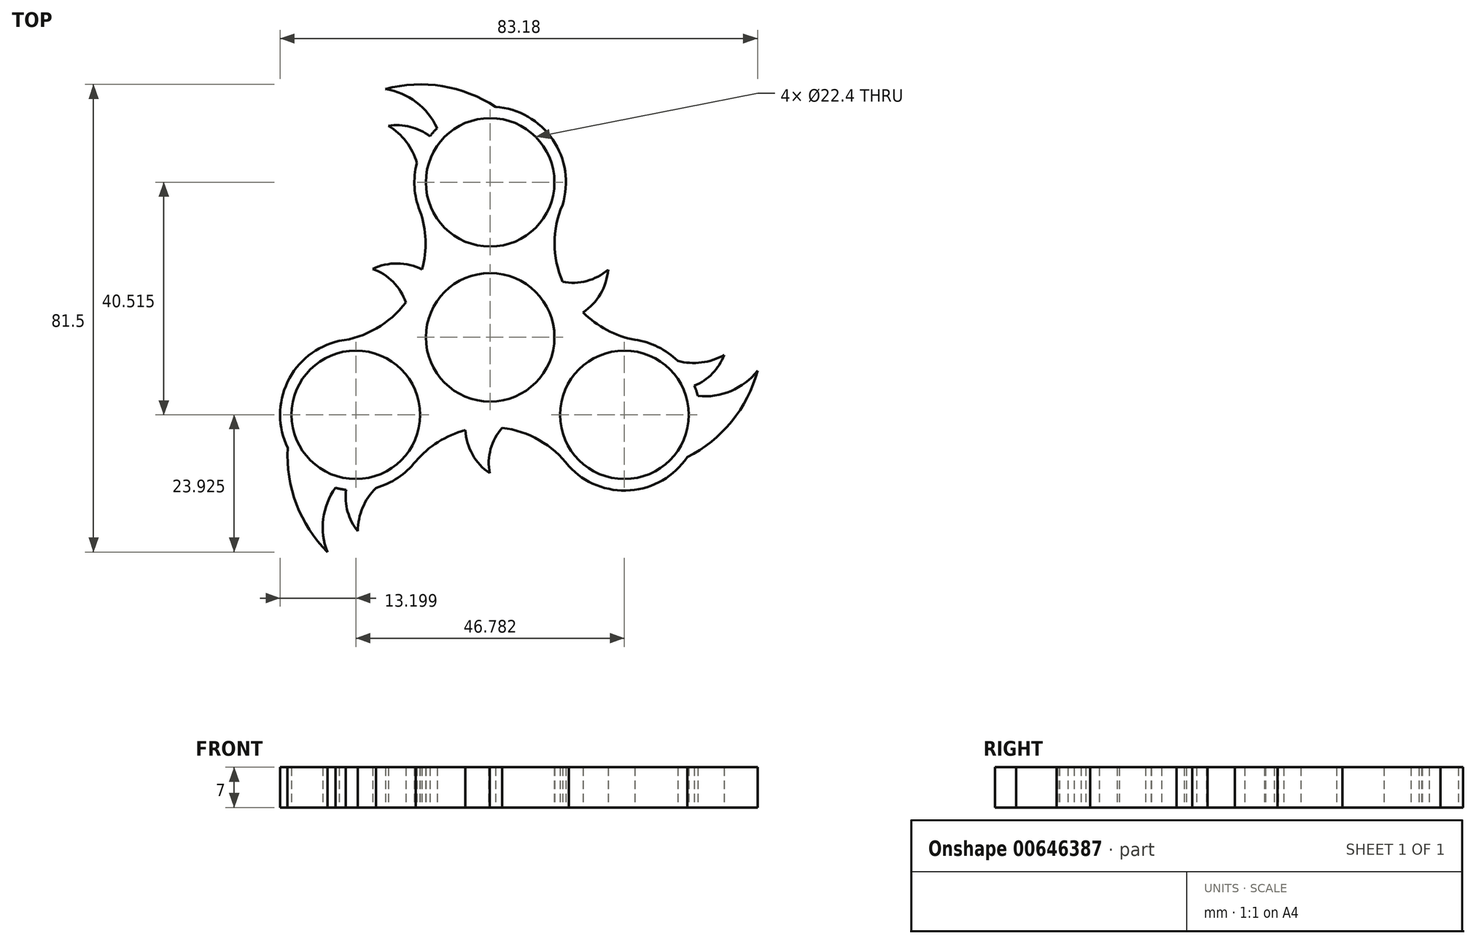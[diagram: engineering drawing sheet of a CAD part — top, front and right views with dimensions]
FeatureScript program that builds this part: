
annotation { "Feature Type Name" : "Feature", "Feature Type Description" : "" }
export const myFeature = defineFeature(function(context is Context, id is Id, definition is map)
    precondition{}
    {
        {
            var Q0;
            Q0=qCreatedBy(makeId("Top.planeOp"),FACE);
            var sketch = newSketch(context, id + "F0", { "sketchPlane" : qUnion([Q0])});
            skCircle(sketch, "E0", {"center": v(0, 0) * mm, "radius": 11.2 * mm});
            skCircle(sketch, "E1", {"center": v(0, 27) * mm, "radius": 11.2 * mm});
            skArc(sketch, "E2", {"start": v(12.09, 21.7) * mm, "mid": v(11.3, 33.83) * mm, "end": v(0.93, 40.18) * mm});
            skCircle(sketch, "E3.1.0", {"center": v(-23.4, -13.5) * mm, "radius": 11.2 * mm});
            skArc(sketch, "E3.1.1", {"start": v(-24.84, -0.38) * mm, "mid": v(-34.95, -7.13) * mm, "end": v(-35.26, -19.29) * mm});
            skCircle(sketch, "E3.2.0", {"center": v(23.4, -13.5) * mm, "radius": 11.2 * mm});
            skArc(sketch, "E3.2.1", {"start": v(12.75, -21.32) * mm, "mid": v(23.65, -26.7) * mm, "end": v(34.33, -20.9) * mm});
            skArc(sketch, "E4", {"start": v(34.33, -20.9) * mm, "mid": v(42.07, -14.67) * mm, "end": v(46.59, -5.84) * mm});
            skArc(sketch, "E5", {"start": v(36.18, -10.22) * mm, "mid": v(41.94, -9.35) * mm, "end": v(46.59, -5.84) * mm});
            skArc(sketch, "E6", {"start": v(35.58, -8.44) * mm, "mid": v(38.73, -6.3) * mm, "end": v(40.78, -3.07) * mm});
            skArc(sketch, "E7", {"start": v(32.67, -4.11) * mm, "mid": v(36.82, -4.39) * mm, "end": v(40.78, -3.07) * mm});
            skArc(sketch, "E8.1.0", {"start": v(0.93, 40.18) * mm, "mid": v(-8.33, 43.77) * mm, "end": v(-18.24, 43.27) * mm});
            skArc(sketch, "E8.1.1", {"start": v(-9.24, 36.44) * mm, "mid": v(-12.87, 41) * mm, "end": v(-18.24, 43.27) * mm});
            skArc(sketch, "E8.1.2", {"start": v(-10.48, 35.04) * mm, "mid": v(-13.92, 36.69) * mm, "end": v(-17.73, 36.85) * mm});
            skArc(sketch, "E8.1.3", {"start": v(-12.77, 30.35) * mm, "mid": v(-14.61, 34.08) * mm, "end": v(-17.73, 36.85) * mm});
            skArc(sketch, "E8.2.0", {"start": v(-35.26, -19.29) * mm, "mid": v(-33.74, -29.1) * mm, "end": v(-28.35, -37.43) * mm});
            skArc(sketch, "E8.2.1", {"start": v(-26.94, -26.22) * mm, "mid": v(-29.07, -31.64) * mm, "end": v(-28.35, -37.43) * mm});
            skArc(sketch, "E8.2.2", {"start": v(-25.1, -26.6) * mm, "mid": v(-24.82, -30.4) * mm, "end": v(-23.05, -33.78) * mm});
            skArc(sketch, "E8.2.3", {"start": v(-19.9, -26.23) * mm, "mid": v(-22.21, -29.7) * mm, "end": v(-23.05, -33.78) * mm});
            skArc(sketch, "E9", {"start": v(12.6, 23.07) * mm, "mid": v(11.24, 16.38) * mm, "end": v(12.6, 9.7) * mm});
            skArc(sketch, "E10.1.0", {"start": v(-26.28, -0.63) * mm, "mid": v(-19.8, 1.54) * mm, "end": v(-14.7, 6.07) * mm});
            skArc(sketch, "E10.2.0", {"start": v(13.68, -22.45) * mm, "mid": v(8.57, -17.93) * mm, "end": v(2.09, -15.76) * mm});
            skArc(sketch, "E11", {"start": v(16.19, 4.36) * mm, "mid": v(19.23, 7.56) * mm, "end": v(20.55, 11.78) * mm});
            skArc(sketch, "E12", {"start": v(12.6, 9.7) * mm, "mid": v(16.82, 9.81) * mm, "end": v(20.55, 11.78) * mm});
            skArc(sketch, "E13.1.0", {"start": v(-11.87, 11.84) * mm, "mid": v(-16.16, 12.87) * mm, "end": v(-20.47, 11.9) * mm});
            skArc(sketch, "E13.1.1", {"start": v(-14.7, 6.07) * mm, "mid": v(-16.9, 9.66) * mm, "end": v(-20.47, 11.9) * mm});
            skArc(sketch, "E13.2.0", {"start": v(-4.32, -16.2) * mm, "mid": v(-3.07, -20.43) * mm, "end": v(-0.07, -23.68) * mm});
            skArc(sketch, "E13.2.1", {"start": v(2.09, -15.76) * mm, "mid": v(0.09, -19.47) * mm, "end": v(-0.07, -23.68) * mm});
            skArc(sketch, "E14.trimOffspring", {"start": v(16.19, 4.36) * mm, "mid": v(20.33, 1.28) * mm, "end": v(25.2, -0.43) * mm});
            skArc(sketch, "E15.trimOffspring", {"start": v(-11.87, 11.84) * mm, "mid": v(-11.27, 16.97) * mm, "end": v(-12.23, 22.04) * mm});
            skArc(sketch, "E16.trimOffspring", {"start": v(-26.94, -26.22) * mm, "mid": v(-26.03, -26.44) * mm, "end": v(-25.1, -26.6) * mm});
            skArc(sketch, "E17.trimOffspring", {"start": v(-19.9, -26.23) * mm, "mid": v(-16.06, -24.48) * mm, "end": v(-12.98, -21.61) * mm});
            skArc(sketch, "E18.trimOffspring", {"start": v(-4.32, -16.2) * mm, "mid": v(-9.06, -18.25) * mm, "end": v(-12.98, -21.61) * mm});
            skArc(sketch, "E19.trimOffspring", {"start": v(36.18, -10.22) * mm, "mid": v(35.91, -9.32) * mm, "end": v(35.58, -8.44) * mm});
            skArc(sketch, "E20.trimOffspring", {"start": v(32.67, -4.11) * mm, "mid": v(29.23, -1.67) * mm, "end": v(25.2, -0.43) * mm});
            skArc(sketch, "E21.trimOffspring", {"start": v(-9.24, 36.44) * mm, "mid": v(-9.88, 35.76) * mm, "end": v(-10.48, 35.04) * mm});
            skArc(sketch, "E22.trimOffspring", {"start": v(-12.77, 30.35) * mm, "mid": v(-13.17, 26.15) * mm, "end": v(-12.23, 22.04) * mm});
            skSolve(sketch);
        }
        {
            var Q0;
            Q0=makeQuery(id+"F0.imprint","IMPRINT",FACE,{"disambiguationData":[TD([[makeQuery(id+"F0.imprint","IMPRINT",EDGE,{"derivedFrom":sQuery(id+"F0.wireOp",EDGE,"E0")}),-1.0]])]});
            extrude(context, id + "F1", {"entities" : qUnion([Q0]), "depth" : 7 * mm, "offsetDistance" : 25 * mm});
        }
    });
